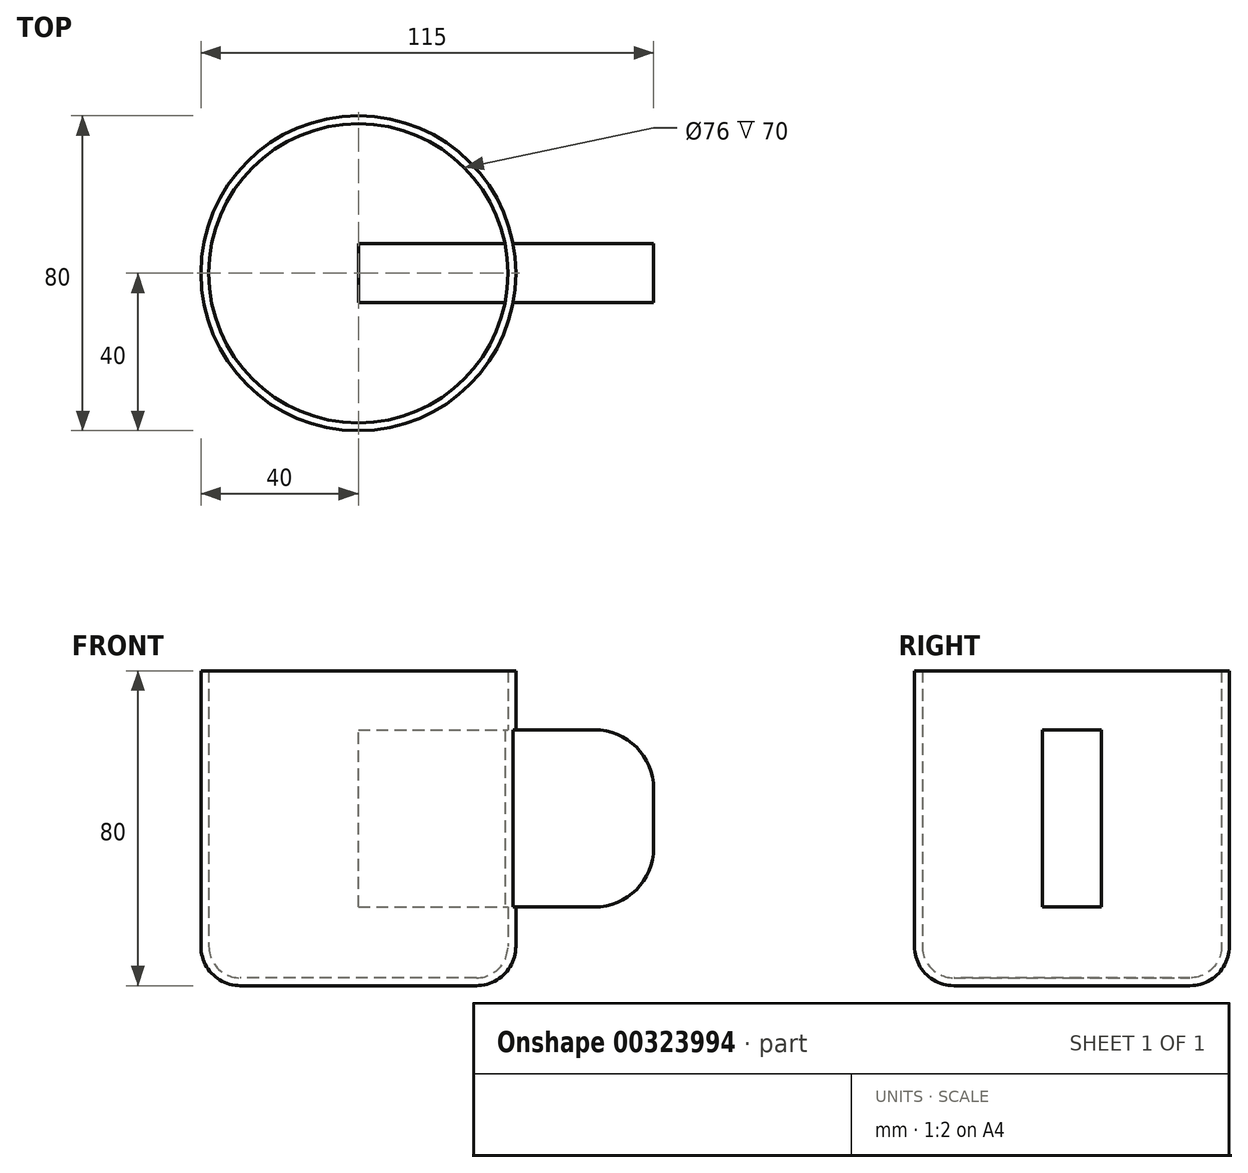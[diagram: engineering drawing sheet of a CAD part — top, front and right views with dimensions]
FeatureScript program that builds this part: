
annotation { "Feature Type Name" : "Feature", "Feature Type Description" : "" }
export const myFeature = defineFeature(function(context is Context, id is Id, definition is map)
    precondition{}
    {
        {
            var Q0;
            Q0=qCreatedBy(makeId("Top.planeOp"),FACE);
            var sketch = newSketch(context, id + "F0", { "sketchPlane" : qUnion([Q0])});
            skCircle(sketch, "E0", {"center": v(0, 0) * mm, "radius": 40 * mm});
            skSolve(sketch);
        }
        {
            var Q0;
            Q0=makeQuery(id+"F0.imprint","IMPRINT",FACE,{"disambiguationData":[TD([[makeQuery(id+"F0.imprint","IMPRINT",EDGE,{"derivedFrom":sQuery(id+"F0.wireOp",EDGE,"E0")}),1.0]])]});
            extrude(context, id + "F1", {"entities" : qUnion([Q0]), "depth" : 80 * mm});
        }
        {
            var Q0;
            Q0=makeQuery(id+"F1.opExtrude","CAP_EDGE",EDGE,{"disambiguationData":[OSD([sQuery(id+"F0.wireOp",EDGE,"E0")])],"isStart":true});
            fillet(context, id + "F2", {"entities" : qUnion([Q0]), "radius" : 10 * mm, "tangentPropagation" : true, "allowEdgeOverflow" : false});
        }
        {
            var Q0;
            Q0=makeQuery(id+"F1.opExtrude","CAP_FACE",FACE,{"disambiguationData":[OSD([sQuery(id+"F0.wireOp",EDGE,"E0")])],"isStart":false});
            shell(context, id + "F3", {"entities" : qUnion([Q0]), "thickness" : 2 * mm});
        }
        {
            var Q0;
            Q0=qCreatedBy(makeId("Front.planeOp"),FACE);
            var sketch = newSketch(context, id + "F4", { "sketchPlane" : qUnion([Q0])});
            skLineSegment(sketch, "E1.bottom", {"start": v(0, 20) * mm, "end": v(75, 20) * mm});
            skLineSegment(sketch, "E1.top", {"start": v(0, 65) * mm, "end": v(75, 65) * mm});
            skLineSegment(sketch, "E1.left", {"start": v(0, 20) * mm, "end": v(0, 65) * mm});
            skLineSegment(sketch, "E1.right", {"start": v(75, 20) * mm, "end": v(75, 65) * mm});
            skSolve(sketch);
        }
        {
            var Q0;
            Q0=makeQuery(id+"F4.imprint","IMPRINT",FACE,{"disambiguationData":[TD([[makeQuery(id+"F4.imprint","IMPRINT",EDGE,{"derivedFrom":sQuery(id+"F4.wireOp",EDGE,"E1.bottom")}),1.0]])]});
            extrude(context, id + "F5", {"entities" : qUnion([Q0]), "operationType" : NewBodyOperationType.ADD, "endBound" : BoundingType.SYMMETRIC, "depth" : 15 * mm});
        }
        {
            var Q0;
            Q0=makeQuery(id+"F5.opExtrude","SWEPT_EDGE",EDGE,{"disambiguationData":[OSD([sQuery(id+"F4.wireOp",EDGE,"E1.top"),sQuery(id+"F4.wireOp",EDGE,"E1.right")])]});
            var Q1;
            Q1=makeQuery(id+"F5.opExtrude","SWEPT_EDGE",EDGE,{"disambiguationData":[OSD([sQuery(id+"F4.wireOp",EDGE,"E1.bottom"),sQuery(id+"F4.wireOp",EDGE,"E1.right")])]});
            fillet(context, id + "F6", {"entities" : qUnion([Q0, Q1]), "radius" : 15 * mm, "tangentPropagation" : true, "allowEdgeOverflow" : false});
        }
    });
